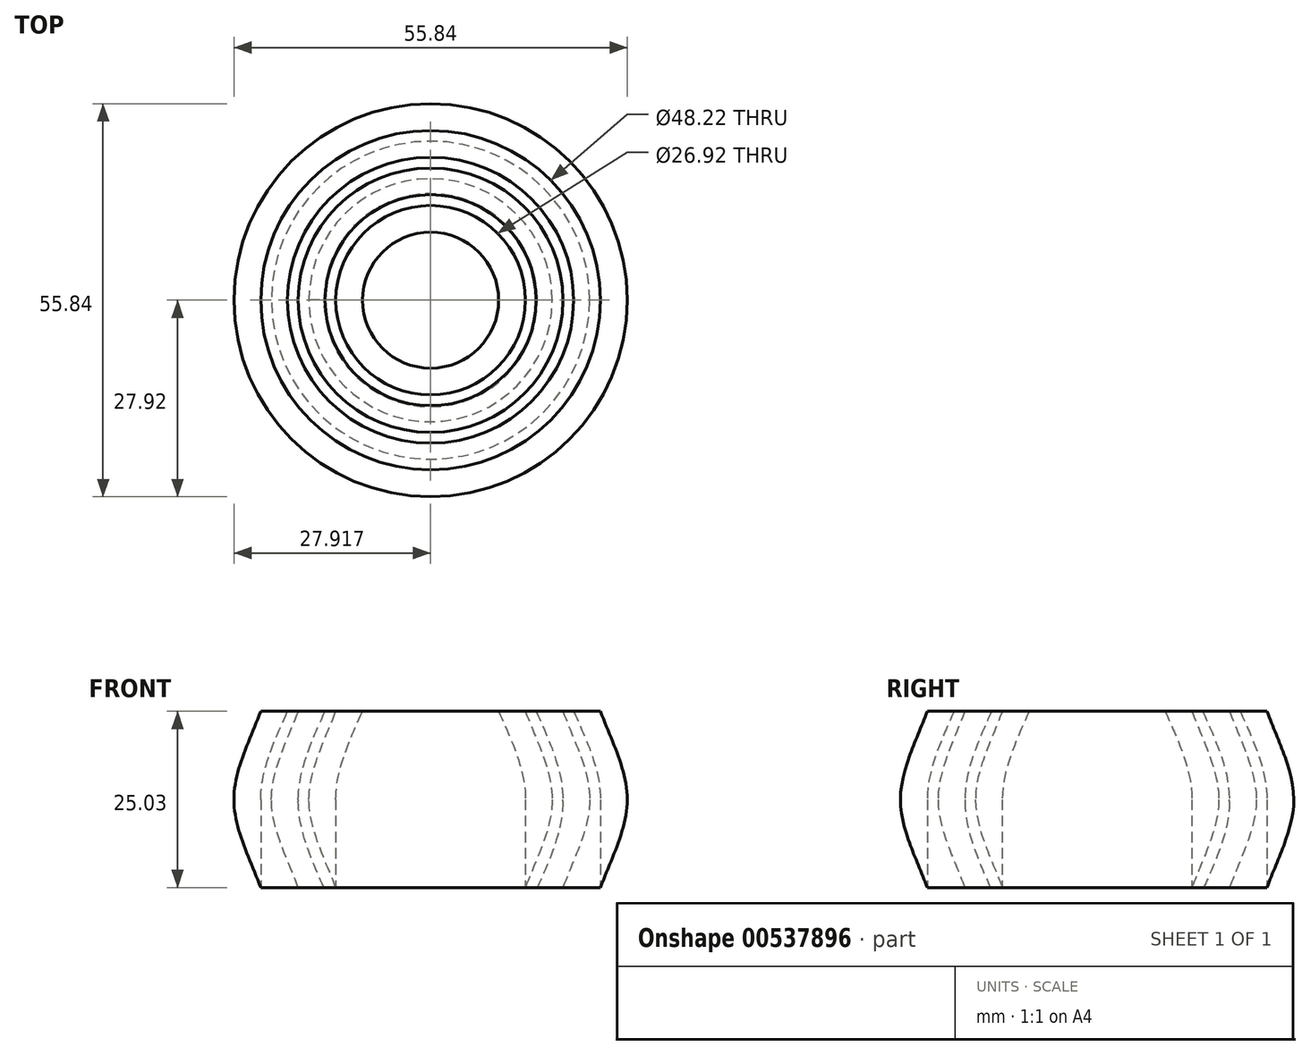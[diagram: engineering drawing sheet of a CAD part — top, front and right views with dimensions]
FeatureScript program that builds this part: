
annotation { "Feature Type Name" : "Feature", "Feature Type Description" : "" }
export const myFeature = defineFeature(function(context is Context, id is Id, definition is map)
    precondition{}
    {
        {
            var Q0;
            Q0=qCreatedBy(makeId("Front.planeOp"),FACE);
            var sketch = newSketch(context, id + "F0", { "sketchPlane" : qUnion([Q0])});
            skLineSegment(sketch, "E0", {"start": v(6.35, 3.06) * mm, "end": v(0, 3.06) * mm});
            skLineSegment(sketch, "E1", {"start": v(24.25, 3.06) * mm, "end": v(28.05, 3.06) * mm});
            skPoint(sketch, "E2.orphan", {"position": v(31.75, 3.06) * mm});
            skLineSegment(sketch, "E3", {"start": v(28.05, 3.06) * mm, "end": v(28.05, 28.1) * mm});
            skFitSpline(sketch, "E4", {"points": [v(24.25, 3.06) * mm, v(28.05, 15.58) * mm, v(24.25, 28.1) * mm], "startDerivative": vector(11.43, 25.4) * mm, "endDerivative": vector(-11.43, 25.4) * mm});
            skFitSpline(sketch, "E5", {"points": [v(28.05, 3.06) * mm, v(31.86, 15.58) * mm, v(28.05, 28.1) * mm], "startDerivative": vector(9.52, 25.4) * mm, "endDerivative": vector(-9.52, 25.4) * mm});
            skLineSegment(sketch, "E6.trimOffspring", {"start": v(24.25, 28.1) * mm, "end": v(28.05, 28.1) * mm});
            skPoint(sketch, "E7.end.orphan", {"position": v(31.86, 28.1) * mm});
            skPoint(sketch, "E8.orphan", {"position": v(31.86, 3.06) * mm});
            skLineSegment(sketch, "E9.trimOffspring", {"start": v(28.05, 15.58) * mm, "end": v(31.86, 15.58) * mm});
            skLineSegment(sketch, "E10", {"start": v(24.25, 3.06) * mm, "end": v(6.35, 3.06) * mm});
            skLineSegment(sketch, "E11", {"start": v(24.25, 3.06) * mm, "end": v(22.96, 3.06) * mm});
            skLineSegment(sketch, "E12", {"start": v(19.08, 3.06) * mm, "end": v(22.72, 3.06) * mm});
            skPoint(sketch, "E13.orphan", {"position": v(25.43, 3.06) * mm});
            skLineSegment(sketch, "E14", {"start": v(22.72, 3.06) * mm, "end": v(22.72, 28.1) * mm});
            skFitSpline(sketch, "E15", {"points": [v(19.08, 3.06) * mm, v(22.72, 15.58) * mm, v(18.92, 28.1) * mm], "startDerivative": vector(11.43, 25.4) * mm, "endDerivative": vector(-11.43, 25.4) * mm});
            skFitSpline(sketch, "E16", {"points": [v(22.72, 3.06) * mm, v(26.53, 15.58) * mm, v(22.72, 28.1) * mm], "startDerivative": vector(9.52, 25.4) * mm, "endDerivative": vector(-9.53, 25.4) * mm});
            skLineSegment(sketch, "E17.trimOffspring", {"start": v(18.92, 28.1) * mm, "end": v(22.72, 28.1) * mm});
            skPoint(sketch, "E18.end.orphan", {"position": v(26.53, 28.1) * mm});
            skPoint(sketch, "E19.orphan", {"position": v(26.53, 3.06) * mm});
            skLineSegment(sketch, "E20.trimOffspring", {"start": v(22.72, 15.58) * mm, "end": v(26.53, 15.58) * mm});
            skLineSegment(sketch, "E21", {"start": v(19.08, 3.06) * mm, "end": v(17.56, 3.06) * mm});
            skLineSegment(sketch, "E22", {"start": v(13.6, 3.06) * mm, "end": v(17.4, 3.06) * mm});
            skLineSegment(sketch, "E23", {"start": v(17.4, 3.06) * mm, "end": v(17.4, 28.1) * mm});
            skFitSpline(sketch, "E24", {"points": [v(13.6, 3.06) * mm, v(17.4, 15.58) * mm, v(13.6, 28.1) * mm], "startDerivative": vector(11.43, 25.4) * mm, "endDerivative": vector(-11.43, 25.4) * mm});
            skFitSpline(sketch, "E25", {"points": [v(17.4, 3.06) * mm, v(21.2, 15.58) * mm, v(17.4, 28.1) * mm], "startDerivative": vector(9.52, 25.4) * mm, "endDerivative": vector(-9.53, 25.4) * mm});
            skLineSegment(sketch, "E26.trimOffspring", {"start": v(13.6, 28.1) * mm, "end": v(17.4, 28.1) * mm});
            skPoint(sketch, "E27.end.orphan", {"position": v(21.2, 28.1) * mm});
            skPoint(sketch, "E28.orphan", {"position": v(21.2, 3.06) * mm});
            skLineSegment(sketch, "E29.trimOffspring", {"start": v(17.4, 15.58) * mm, "end": v(21.2, 15.58) * mm});
            skLineSegment(sketch, "E30", {"start": v(4.2, 3.06) * mm, "end": v(3.94, 3.06) * mm});
            skLineSegment(sketch, "E31", {"start": v(0, 0) * mm, "end": v(0, 43.72) * mm});
            skLineSegment(sketch, "E32", {"start": v(3.94, 3.06) * mm, "end": v(3.94, 34.02) * mm});
            skSolve(sketch);
        }
        {
            var Q0;
            {var subQ0=sQuery(id+"F0.wireOp",EDGE,"c6cbf438-6f91-46b9-94fb-a8acab6ed115.trimOffspring");Q0=makeQuery(id+"F0.imprint","IMPRINT",FACE,{"disambiguationData":[TD([[makeQuery(id+"F0.imprint","IMPRINT",EDGE,{"derivedFrom":subQ0}),-1.0]])]});}
            var Q1;
            {var subQ3=sQuery(id+"F0.wireOp",EDGE,"67c426a9-44b4-418a-bda5-b824597e67d5.trimOffspring");Q1=makeQuery(id+"F0.imprint","IMPRINT",FACE,{"disambiguationData":[TD([[makeQuery(id+"F0.imprint","IMPRINT",EDGE,{"derivedFrom":subQ3}),1.0]])]});}
            var Q2;
            {var subQ3=sQuery(id+"F0.wireOp",EDGE,"67c426a9-44b4-418a-bda5-b824597e67d5.trimOffspring");Q2=makeQuery(id+"F0.imprint","IMPRINT",FACE,{"disambiguationData":[TD([[makeQuery(id+"F0.imprint","IMPRINT",EDGE,{"derivedFrom":subQ3}),-1.0]])]});}
            var Q3;
            {var subQ0=sQuery(id+"F0.wireOp",EDGE,"0a6e29e3-f920-4f87-839e-6fa51f2de360.trimOffspring");Q3=makeQuery(id+"F0.imprint","IMPRINT",FACE,{"disambiguationData":[TD([[makeQuery(id+"F0.imprint","IMPRINT",EDGE,{"derivedFrom":subQ0}),1.0]])]});}
            var Q4;
            {var subQ0=sQuery(id+"F0.wireOp",EDGE,"E22");Q4=makeQuery(id+"F0.imprint","IMPRINT",FACE,{"disambiguationData":[TD([[makeQuery(id+"F0.imprint","IMPRINT",EDGE,{"derivedFrom":subQ0}),1.0]])]});}
            var Q5;
            {var subQ3=sQuery(id+"F0.wireOp",EDGE,"E29.trimOffspring");Q5=makeQuery(id+"F0.imprint","IMPRINT",FACE,{"disambiguationData":[TD([[makeQuery(id+"F0.imprint","IMPRINT",EDGE,{"derivedFrom":subQ3}),-1.0]])]});}
            var Q6;
            {var subQ3=sQuery(id+"F0.wireOp",EDGE,"E29.trimOffspring");Q6=makeQuery(id+"F0.imprint","IMPRINT",FACE,{"disambiguationData":[TD([[makeQuery(id+"F0.imprint","IMPRINT",EDGE,{"derivedFrom":subQ3}),1.0]])]});}
            var Q7;
            {var subQ0=sQuery(id+"F0.wireOp",EDGE,"E26.trimOffspring");Q7=makeQuery(id+"F0.imprint","IMPRINT",FACE,{"disambiguationData":[TD([[makeQuery(id+"F0.imprint","IMPRINT",EDGE,{"derivedFrom":subQ0}),-1.0]])]});}
            var Q8;
            {var subQ0=sQuery(id+"F0.wireOp",EDGE,"E17.trimOffspring");Q8=makeQuery(id+"F0.imprint","IMPRINT",FACE,{"disambiguationData":[TD([[makeQuery(id+"F0.imprint","IMPRINT",EDGE,{"derivedFrom":subQ0}),-1.0]])]});}
            var Q9;
            {var subQ3=sQuery(id+"F0.wireOp",EDGE,"E20.trimOffspring");Q9=makeQuery(id+"F0.imprint","IMPRINT",FACE,{"disambiguationData":[TD([[makeQuery(id+"F0.imprint","IMPRINT",EDGE,{"derivedFrom":subQ3}),1.0]])]});}
            var Q10;
            {var subQ3=sQuery(id+"F0.wireOp",EDGE,"E20.trimOffspring");Q10=makeQuery(id+"F0.imprint","IMPRINT",FACE,{"disambiguationData":[TD([[makeQuery(id+"F0.imprint","IMPRINT",EDGE,{"derivedFrom":subQ3}),-1.0]])]});}
            var Q11;
            {var subQ0=sQuery(id+"F0.wireOp",EDGE,"E12");var subQ3=sQuery(id+"F0.wireOp",EDGE,"E15");var subQ5=makeQuery(id+"F0.imprint","INTERSECT",VERTEX,{"derivedFrom":[subQ3,subQ0]});Q11=makeQuery(id+"F0.imprint","IMPRINT",FACE,{"disambiguationData":[TD([[makeQuery(id+"F0.imprint","IMPRINT",EDGE,{"disambiguationData":[TD([[subQ5,-1.0]])],"derivedFrom":subQ3}),-1.0]])]});}
            var Q12;
            {var subQ0=sQuery(id+"F0.wireOp",EDGE,"E1");Q12=makeQuery(id+"F0.imprint","IMPRINT",FACE,{"disambiguationData":[TD([[makeQuery(id+"F0.imprint","IMPRINT",EDGE,{"derivedFrom":subQ0}),1.0]])]});}
            var Q13;
            {var subQ0=sQuery(id+"F0.wireOp",EDGE,"E6.trimOffspring");Q13=makeQuery(id+"F0.imprint","IMPRINT",FACE,{"disambiguationData":[TD([[makeQuery(id+"F0.imprint","IMPRINT",EDGE,{"derivedFrom":subQ0}),-1.0]])]});}
            var Q14;
            {var subQ3=sQuery(id+"F0.wireOp",EDGE,"E9.trimOffspring");Q14=makeQuery(id+"F0.imprint","IMPRINT",FACE,{"disambiguationData":[TD([[makeQuery(id+"F0.imprint","IMPRINT",EDGE,{"derivedFrom":subQ3}),-1.0]])]});}
            var Q15;
            {var subQ3=sQuery(id+"F0.wireOp",EDGE,"E9.trimOffspring");Q15=makeQuery(id+"F0.imprint","IMPRINT",FACE,{"disambiguationData":[TD([[makeQuery(id+"F0.imprint","IMPRINT",EDGE,{"derivedFrom":subQ3}),1.0]])]});}
            var Q16;
            Q16=sQuery(id+"F0.wireOp",EDGE,"E32");
            revolve(context, id + "F1", {"entities" : qUnion([Q0, Q1, Q2, Q3, Q4, Q5, Q6, Q7, Q8, Q9, Q10, Q11, Q12, Q13, Q14, Q15]), "axis" : qUnion([Q16]), "revolveType" : RevolveType.FULL});
        }
    });
